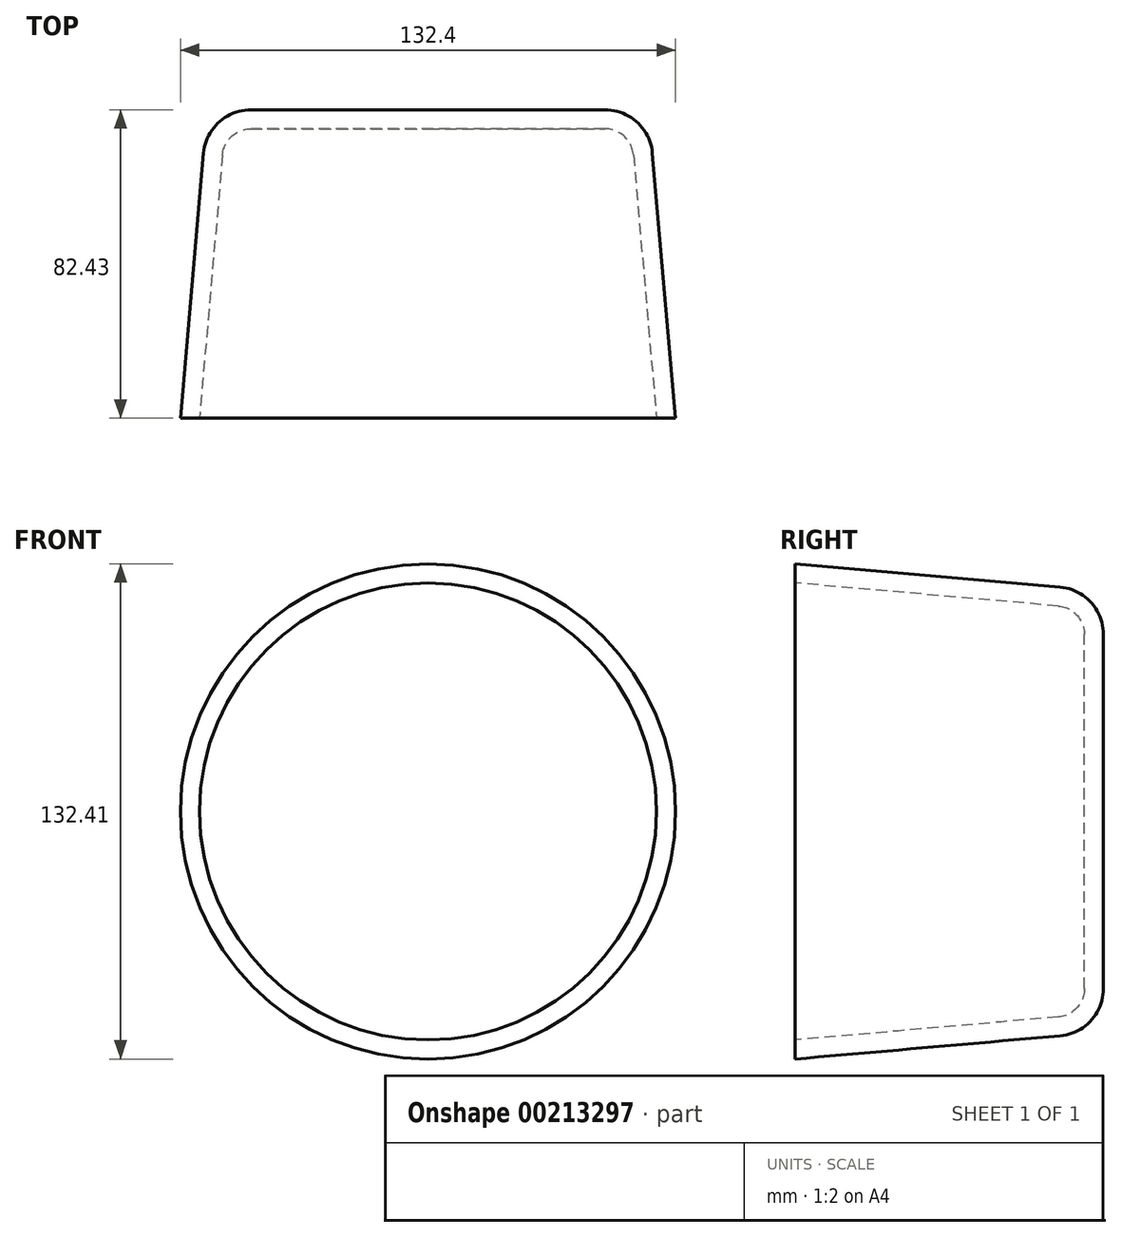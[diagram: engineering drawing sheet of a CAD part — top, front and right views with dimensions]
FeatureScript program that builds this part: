
annotation { "Feature Type Name" : "Feature", "Feature Type Description" : "" }
export const myFeature = defineFeature(function(context is Context, id is Id, definition is map)
    precondition{}
    {
        {
            var Q0;
            Q0=qCreatedBy(makeId("Front.planeOp"),FACE);
            var sketch = newSketch(context, id + "F0", { "sketchPlane" : qUnion([Q0])});
            skCircle(sketch, "E0", {"center": v(0, 46.28) * mm, "radius": 59 * mm});
            skSolve(sketch);
        }
        {
            var Q0;
            Q0=makeQuery(id+"F0.imprint","IMPRINT",FACE,{"disambiguationData":[TD([[makeQuery(id+"F0.imprint","IMPRINT",EDGE,{"derivedFrom":sQuery(id+"F0.wireOp",EDGE,"E0")}),1.0]])]});
            extrude(context, id + "F4", {"entities" : qUnion([Q0]), "depth" : 82.43 * mm, "hasDraft" : true, "draftAngle" : 5 * degree});
        }
        {
            var Q0;
            Q0=makeQuery(id+"F4.opExtrude","CAP_EDGE",EDGE,{"disambiguationData":[OSD([sQuery(id+"F0.wireOp",EDGE,"E0")])],"isStart":true});
            fillet(context, id + "F1", {"entities" : qUnion([Q0]), "radius" : 12.7 * mm, "tangentPropagation" : true, "allowEdgeOverflow" : false});
        }
        {
            var Q0;
            Q0=makeQuery(id+"F4.opExtrude","CAP_FACE",FACE,{"disambiguationData":[OSD([sQuery(id+"F0.wireOp",EDGE,"E0")])],"isStart":false});
            shell(context, id + "F2", {"entities" : qUnion([Q0]), "thickness" : 5.08 * mm});
        }
    });
